# Revit family: HERZ Strömax Commissioning Valve With Integral Fixed orifice Plate 4017 ML
name_source: partatom
category: Rohrzubehör
units: mm (PartAtom-declared; Revit-internal decimal feet)

## family parameters
Arbeitsebenenbasiert = Nein
Beim Laden mit Abzugskörper schneiden = Nein
Bemaßung runder Anschluss = Durchmesser verwenden
Gemeinsam genutzt = Nein
Immer vertikal = Ja
OmniClass-Nummer = 23.65.55.14
OmniClass-Titel = Valves for Liquid Services
Teiletyp = Unterbricht

## types (1)
- HERZ Strömax Commissioning Valve With Integral Fixed orifice Plate 4017 ML
    Body = DZR brass
    E00 = 0 mm  [stored 0 ft]
    Field of application = Can be used as isolating and commissioning valve.
    H02 = 13 mm
    Hersteller = HERZ Armaturen Ges.m.b.H.
    Max. differential pressure at closed valve = 1000000.0 Pa
    Max. operating pressure = 2000000.0 Pa
    Max. operating temperature = 130 °C
    Medium = Water purity in accordance with the OeNORM H5195 and VDI 2035 standards.
Ethylene and propylene glycol can be mixed to a ratio of 25 - 50 vol. %.
    Model = STRÖMAX 4017 ML, commissioning valve in Y pattern with an orifice plate and an connection for impulse line for differential pressure measurement, with test points:
DZR brass, female threaded ends, non-rising stem sealed with Triple-O-Ring, presetting through stroke limiting, handwhell with presetting digital display.
    R01 = 12 mm  [stored 0.0393701 ft]
    R02 = 9.5 mm  [stored 0.031168 ft]
    R03 = 21.5 mm
    S03 = 60 mm  [stored 0.19685 ft]
    SCRNCODE = 05;07;02
    SCRNSEQ = ARM;ARM_TYP="STRV";2
    SW01 = 60.00°
    URL = www.herzvalves.com
    Vorgabe-Ansicht = 0 mm  [stored 0 ft]
    W01 = 50.00°

note: [stored X ft] marks values corroborated as IEEE doubles in the binary element streams (Revit-internal decimal feet)
